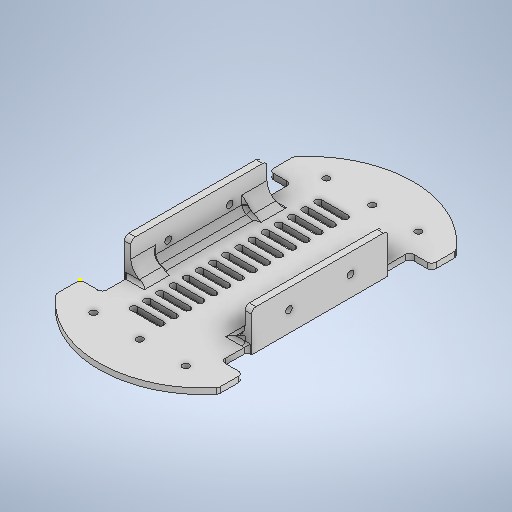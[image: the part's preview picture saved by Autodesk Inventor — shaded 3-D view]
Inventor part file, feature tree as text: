
AUTODESK INVENTOR PART (.ipt)
format: ipt  version: 2025.2 (Build 292293000, 293)  size: 808,448 bytes
history: native  units: mm
features: fillet x34, sketch x14, extrude x12
ambient origin geometry x8: Origin, YZ Plane, XZ Plane, XY Plane, X Axis, Y Axis, Z Axis, Center Point
bodies: Solid1 (feature_tree)
feature tree (60):
  extrude  "Extrusion1"  Depth=11.0mm
  fillet  "Face Fillet1"
  fillet  "Face Fillet2"
  fillet  "Face Fillet3"
  fillet  "Face Fillet4"
  fillet  "Face Fillet5"
  fillet  "Face Fillet6"
  fillet  "Face Fillet7"
  fillet  "Face Fillet8"
  fillet  "Face Fillet9"
  fillet  "Face Fillet10"
  fillet  "Face Fillet11"
  fillet  "Face Fillet12"
  sketch  "Sketch5"  dims[d3=11.0mm d4=17.5mm]
  sketch  "Sketch6"  dims[d5=17.5mm d11=74.0mm]
  sketch  "Sketch7"  dims[d12=74.0mm d15=27.0mm]
  sketch  "Sketch8"  dims[d16=27.0mm d17=2.6mm d18=0.0mm]
  sketch  "Sketch9"  dims[d19=2.0mm d20=2.0mm]
  extrude  "Extrusion5"  Depth=17.5mm
  extrude  "Extrusion6"  Depth=74.0mm
  extrude  "Extrusion7"  Depth=74.0mm
  extrude  "Extrusion8"  Depth=2.6mm TaperAngle=0.0deg
  sketch  "Sketch13"  dims[d25=2.0mm d26=2.0mm]
  sketch  "Sketch14"  dims[d27=2.0mm d48=2.0mm]
  extrude  "Extrusion9"  Depth=2.0mm
  extrude  "Extrusion10"  Depth=2.0mm
  fillet  "Face Fillet13"
  fillet  "Face Fillet14"
  fillet  "Face Fillet15"
  fillet  "Face Fillet16"
  extrude  "Extrusion12"  Depth=2.0mm
  extrude  "Extrusion14"  Depth=2.0mm
  sketch  "Sketch16"  dims[d63=1.5mm d65=21.0mm d66=21.0mm d67=10.0mm d68=2.9mm d69=2.9mm d70=2.9mm d71=10.0mm d72=3.0mm d73=3.0mm d74=3.0mm d87=18.0mm d88=82.0mm]
  extrude  "Extrusion15"  Depth=2.0mm
  extrude  "Extrusion16"  Depth=2.0mm
  extrude  "Extrusion17"  Depth=3.0mm
  fillet  "Fillet1"  Radius=21.0mm
  fillet  "Fillet2"  Radius=10.0mm
  fillet  "Fillet3"  Radius=2.9mm
  fillet  "Face Fillet19"
  fillet  "Face Fillet20"
  fillet  "Face Fillet21"
  fillet  "Face Fillet22"
  fillet  "Face Fillet23"
  fillet  "Face Fillet24"
  fillet  "Face Fillet25"
  fillet  "Fillet4"  Radius=2.9mm
  fillet  "Fillet5"  Radius=2.9mm
  fillet  "Fillet6"  Radius=10.0mm
  fillet  "Fillet8"  Radius=3.0mm
  fillet  "Fillet9"  Radius=3.0mm
  fillet  "Fillet10"  Radius=3.0mm
  fillet  "Fillet11"  Radius=18.0mm
  fillet  "Fillet12"  Radius=82.0mm
  sketch  "Sketch1"  dims[d1=86.0mm d2=11.0mm]
  sketch  "Sketch10"  dims[d21=2.0mm d22=2.0mm]
  sketch  "Sketch11"  dims[d23=2.0mm d24=2.0mm]
  sketch  "Sketch15"  dims[d49=2.0mm d50=2.0mm]
  sketch  "Sketch17"  dims[d89=31.0mm]
  sketch  "Sketch18"  dims[d90=31.0mm d91=31.0mm d92=18.0mm d93=2.0mm d94=0.0mm d95=2.0mm d96=0.0mm d97=1.0mm d98=0.0mm d99=1.0mm d100=0.0mm d101=14.0mm d102=14.0mm d103=18.0mm d104=9.3mm d105=9.3mm d106=3.0mm d107=3.0mm d108=3.0mm d109=3.0mm d110=40.0mm d111=0.0mm d112=40.0mm d113=0.0mm d114=2.0mm d115=2.0mm d116=2.0mm d117=2.0mm d120=10.0mm d121=0.0mm d125=86.0mm d126=0.5mm d127=0.5mm d128=12.0mm d129=15.0mm d130=3.0mm d131=3.0mm d132=3.0mm d133=3.0mm d134=3.0mm d135=3.0mm d136=3.0mm d137=3.0mm d138=3.0mm d139=3.0mm d140=3.0mm d141=3.0mm d142=3.0mm d143=3.0mm d144=3.0mm d145=3.0mm d146=3.0mm d147=3.0mm d148=3.0mm d149=3.0mm d150=3.0mm d151=3.0mm d152=3.0mm d153=3.0mm d154=3.0mm d155=3.0mm d156=3.0mm d157=3.0mm d158=3.0mm d159=40.0mm d160=0.0mm d163=1.5mm d164=1.5mm d165=13.5mm d166=13.5mm d167=1.5mm d168=9.0mm d169=4.0mm d170=9.0mm d171=4.0mm d172=4.0mm d173=9.0mm d174=9.0mm d175=10.0mm d176=0.0mm d177=10.0mm d178=0.0mm d179=5.0mm d180=5.0mm d181=45.0mm d182=0.0mm d183=6.67mm d184=6.67mm d185=6.67mm d186=6.67mm d187=3.0mm d188=3.0mm d189=1.4mm d190=1.4mm d191=1.4mm d192=1.4mm d193=1.4mm d194=1.4mm d195=1.4mm d197=1.4mm d198=1.4mm d199=1.4mm d200=1.4mm d201=1.4mm d122=0.5mm d123=0.872665mm]
